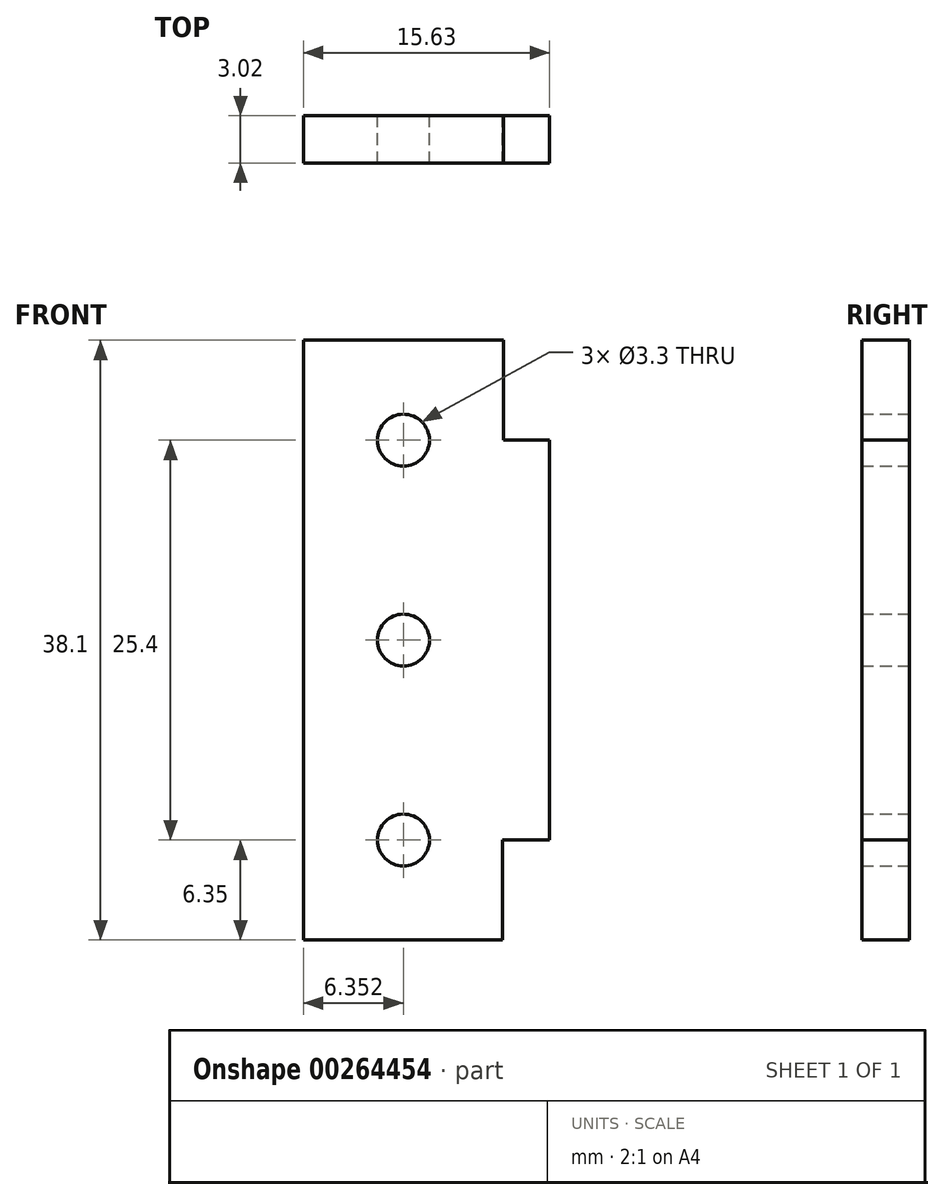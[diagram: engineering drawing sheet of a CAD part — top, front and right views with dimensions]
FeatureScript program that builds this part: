
annotation { "Feature Type Name" : "Feature", "Feature Type Description" : "" }
export const myFeature = defineFeature(function(context is Context, id is Id, definition is map)
    precondition{}
    {
        {
            var Q0;
            Q0=qCreatedBy(makeId("Front.planeOp"),FACE);
            var sketch = newSketch(context, id + "F0", { "sketchPlane" : qUnion([Q0])});
            skLineSegment(sketch, "E0", {"start": v(0, 0) * mm, "end": v(0, -25.4) * mm});
            skLineSegment(sketch, "E1", {"start": v(0, -25.4) * mm, "end": v(-2.97, -25.4) * mm});
            skLineSegment(sketch, "E2", {"start": v(-2.93, 0) * mm, "end": v(0, 0) * mm});
            skLineSegment(sketch, "E3", {"start": v(-2.97, -25.4) * mm, "end": v(-2.97, -31.75) * mm});
            skLineSegment(sketch, "E4", {"start": v(-2.93, 0) * mm, "end": v(-2.93, 6.35) * mm});
            skLineSegment(sketch, "E5", {"start": v(-2.93, 6.35) * mm, "end": v(-15.63, 6.35) * mm});
            skLineSegment(sketch, "E6", {"start": v(-15.63, 6.35) * mm, "end": v(-15.63, -31.75) * mm});
            skLineSegment(sketch, "E7", {"start": v(-15.63, -31.75) * mm, "end": v(-2.97, -31.75) * mm});
            skCircle(sketch, "E8", {"center": v(-9.28, 0) * mm, "radius": 1.65 * mm});
            skPoint(sketch, "E8.centerSnap0", {"position": v(-9.28, 6.35) * mm});
            skCircle(sketch, "E9", {"center": v(-9.28, -25.4) * mm, "radius": 1.65 * mm});
            skCircle(sketch, "E10", {"center": v(-9.28, -12.7) * mm, "radius": 1.65 * mm});
            skPoint(sketch, "E10.centerSnap0", {"position": v(-15.63, -12.7) * mm});
            skSolve(sketch);
        }
        {
            var Q0;
            Q0=makeQuery(id+"F0.imprint","IMPRINT",FACE,{"disambiguationData":[TD([[makeQuery(id+"F0.imprint","IMPRINT",EDGE,{"derivedFrom":sQuery(id+"F0.wireOp",EDGE,"E0")}),-1.0]])]});
            extrude(context, id + "F1", {"entities" : qUnion([Q0]), "depth" : 3.02 * mm});
        }
    });
